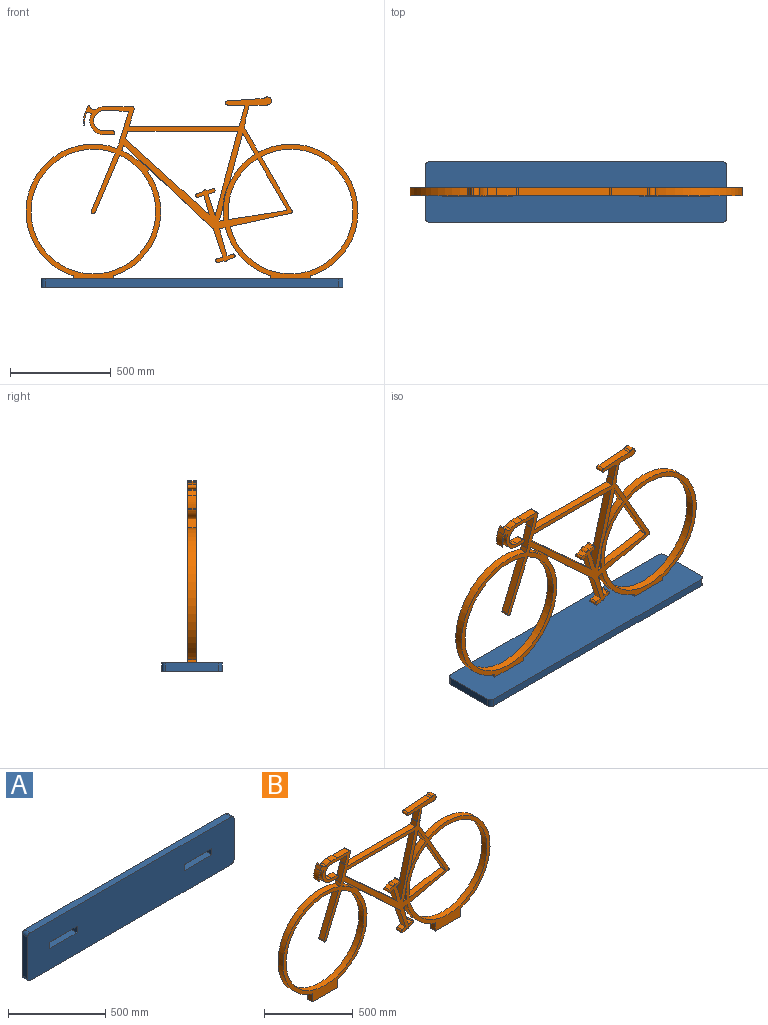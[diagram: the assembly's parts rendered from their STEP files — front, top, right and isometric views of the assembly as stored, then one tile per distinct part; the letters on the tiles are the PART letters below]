
ASSEMBLY  parts=2 mates=1
PART A: 18 faces, bbox 1500x40x300 mm
  f0: plane 200x40mm, normal (0,0,-1), area 8000mm2, adj f1,f15,f16,f17
  f1: plane 40x40mm, normal (-1,0,0), area 1600mm2, adj f0,f2,f16,f17
  f2: plane 200x40mm, normal (0,0,1), area 8000mm2, adj f1,f15,f16,f17
  f3: plane 1460x40mm, normal (0,0,-1), area 58400mm2, adj f4,f13,f16,f17
  f4: cylinder r=20mm len=40mm, axis (0,1,0), area 1256.6mm2, adj f3,f5,f16,f17
  f5: plane 260x40mm, normal (1,0,0), area 10400mm2, adj f4,f6,f16,f17
  f6: cylinder r=20mm len=40mm, axis (0,1,0), area 1256.6mm2, adj f5,f7,f16,f17
  f7: plane 1460x40mm, normal (0,0,1), area 58400mm2, adj f6,f8,f16,f17
  f8: cylinder r=20mm len=40mm, axis (0,1,0), area 1256.6mm2, adj f7,f9,f16,f17
  f9: plane 260x40mm, normal (-1,0,0), area 10400mm2, adj f8,f13,f16,f17
  f10: plane 40x40mm, normal (-1,0,0), area 1600mm2, adj f11,f14,f16,f17
  f11: plane 200x40mm, normal (0,0,1), area 8000mm2, adj f10,f12,f16,f17
  f12: plane 40x40mm, normal (1,0,0), area 1600mm2, adj f11,f14,f16,f17
  f13: cylinder r=20mm len=40mm, axis (0,1,0), area 1256.6mm2, adj f3,f9,f16,f17
  f14: plane 200x40mm, normal (0,0,-1), area 8000mm2, adj f10,f12,f16,f17
  f15: plane 40x40mm, normal (1,0,0), area 1600mm2, adj f0,f2,f16,f17
  f16: plane 1500x300mm, normal (0,-1,0), area 433656.6mm2, adj f0,f1,f2,f3,f4,f5,f6,f7
  f17: plane 1500x300mm, normal (0,1,0), area 433656.6mm2, adj f0,f1,f2,f3,f4,f5,f6,f7
PART B: 105 faces, bbox 1650x40x944.4 mm
  f0: plane 299.62x65.43mm, normal (0.21,0,-0.98), area 12267.2mm2, adj f1,f102,f103,f104
  f1: cylinder r=9mm len=40mm, axis (0,1,0), area 905.8mm2, adj f0,f2,f103,f104
  f2: plane 266.74x152.85mm, normal (0.87,0,0.5), area 12297.2mm2, adj f1,f102,f103,f104
  f3: cylinder r=310mm len=620mm, axis (0,1,0), area 76908.3mm2, adj f4,f96,f103,f104
  f4: plane 286.93x116.93mm, normal (-0.93,0,0.38), area 12393.5mm2, adj f3,f5,f103,f104
  f5: cylinder r=10mm len=40mm, axis (0,1,0), area 1250.1mm2, adj f4,f96,f103,f104
  f6: plane 73.76x69.4mm, normal (-0.69,0,-0.73), area 4051.1mm2, adj f7,f97,f103,f104
  f7: plane 40x7.1mm, normal (-0.73,0,0.69), area 389.9mm2, adj f6,f8,f103,f104
  f8: cylinder r=335mm len=78.04mm, axis (0,1,0), area 3724.8mm2, adj f7,f97,f103,f104
  f9: plane 415.14x377.47mm, normal (0.67,0,0.74), area 22443.7mm2, adj f10,f98,f103,f104
  f10: plane 40x36.4mm, normal (0.96,0,-0.28), area 1517.5mm2, adj f9,f11,f103,f104
  f11: plane 545.63x40mm, normal (0,0,-1), area 21825.3mm2, adj f10,f12,f103,f104
  f12: plane 416.76x111.67mm, normal (-0.97,0,0.26), area 17258.5mm2, adj f11,f13,f103,f104
  f13: plane 104.98x40mm, normal (0.95,0,0.32), area 4426.6mm2, adj f12,f14,f103,f104
  f14: plane 40x27.55mm, normal (0.29,0,-0.96), area 1152.8mm2, adj f13,f15,f103,f104
  f15: cylinder r=10mm len=40mm, axis (0,1,0), area 1256.6mm2, adj f14,f16,f103,f104
  f16: plane 40x27.55mm, normal (-0.29,0,0.96), area 1152.8mm2, adj f15,f17,f103,f104
  f17: cylinder r=15mm len=40mm, axis (0,1,0), area 1009.3mm2, adj f16,f18,f103,f104
  f18: plane 40x27.55mm, normal (-0.29,0,0.96), area 1152.8mm2, adj f17,f19,f103,f104
  f19: cylinder r=10mm len=40mm, axis (0,1,0), area 1256.6mm2, adj f18,f20,f103,f104
  f20: plane 40x27.55mm, normal (0.29,0,-0.96), area 1152.8mm2, adj f19,f98,f103,f104
  f21: plane 235.63x62.8mm, normal (0.97,0,-0.26), area 9754.3mm2, adj f22,f99,f103,f104
  f22: plane 104.53x60.49mm, normal (-0.87,0,-0.5), area 4830.8mm2, adj f21,f23,f103,f104
  f23: cylinder r=335mm len=327.57mm, axis (0,1,0), area 15308.2mm2, adj f22,f24,f103,f104
  f24: plane 40x21.95mm, normal (-0.15,0,0.99), area 888.8mm2, adj f23,f25,f103,f104
  f25: plane 63.96x40mm, normal (0.97,0,-0.26), area 2647.9mm2, adj f24,f99,f103,f104
  f26: cylinder r=3mm len=40mm, axis (0,1,0), area 232.8mm2, adj f27,f100,f103,f104
  f27: plane 286.57x44.86mm, normal (-0.15,0,0.99), area 11602.5mm2, adj f26,f28,f103,f104
  f28: cylinder r=310mm len=302.05mm, axis (0,1,0), area 14106.7mm2, adj f27,f100,f103,f104
  f29: cylinder r=20mm len=40mm, axis (0,1,0), area 189.4mm2, adj f30,f101,f103,f104
  f30: plane 138.94x46.33mm, normal (-0.95,0,-0.32), area 5858.3mm2, adj f29,f31,f103,f104
  f31: plane 40x27.55mm, normal (-0.29,0,0.96), area 1152.8mm2, adj f30,f32,f103,f104
  f32: cylinder r=10mm len=40mm, axis (0,1,0), area 1256.6mm2, adj f31,f33,f103,f104
  f33: plane 40x27.55mm, normal (0.29,0,-0.96), area 1152.8mm2, adj f32,f34,f103,f104
  f34: cylinder r=15mm len=40mm, axis (0,1,0), area 1009.3mm2, adj f33,f35,f103,f104
  f35: plane 40x27.55mm, normal (0.29,0,-0.96), area 1152.8mm2, adj f34,f36,f103,f104
  f36: cylinder r=10mm len=40mm, axis (0,1,0), area 1256.6mm2, adj f35,f37,f103,f104
  f37: plane 40x27.55mm, normal (-0.29,0,0.96), area 1152.8mm2, adj f36,f38,f103,f104
  f38: plane 133.82x40mm, normal (0.96,0,0.27), area 5560.3mm2, adj f37,f39,f103,f104
  f39: plane 40x28.33mm, normal (0.21,0,-0.98), area 1159.9mm2, adj f38,f40,f103,f104
  f40: cylinder r=335mm len=240.06mm, axis (0,1,0), area 13769.4mm2, adj f39,f41,f103,f104
  f41: plane 55.27x40mm, normal (-1,0,0), area 2210.9mm2, adj f40,f42,f103,f104
  f42: plane 200x40mm, normal (0,0,-1), area 8000mm2, adj f41,f43,f103,f104
  f43: plane 55.27x40mm, normal (1,0,0), area 2210.9mm2, adj f42,f44,f103,f104
  f44: cylinder r=335mm len=654.73mm, axis (0,1,0), area 44661.5mm2, adj f43,f45,f103,f104
  f45: plane 123.92x71.01mm, normal (0.87,0,0.5), area 5713.1mm2, adj f44,f46,f103,f104
  f46: plane 40x29.62mm, normal (0.97,0,-0.26), area 1226mm2, adj f45,f47,f103,f104
  f47: plane 40x3.7mm, normal (0.26,0,0.97), area 153.2mm2, adj f46,f48,f103,f104
  f48: plane 78.52x40mm, normal (0.97,0,-0.24), area 3237.8mm2, adj f47,f49,f103,f104
  f49: cylinder r=2mm len=40mm, axis (0,1,0), area 106mm2, adj f48,f50,f103,f104
  f50: plane 89.34x40mm, normal (0,0,-1), area 3573.6mm2, adj f49,f51,f103,f104
  f51: cylinder r=20mm len=40mm, axis (0,1,0), area 3014.9mm2, adj f50,f52,f103,f104
  f52: cylinder r=20mm len=40mm, axis (0,1,0), area 445.9mm2, adj f51,f53,f103,f104
  f53: plane 178.62x40mm, normal (-0.07,0,1), area 7162.1mm2, adj f52,f54,f103,f104
  f54: cylinder r=10mm len=40mm, axis (0,1,0), area 1228.8mm2, adj f53,f55,f103,f104
  f55: plane 85.7x40mm, normal (0,0,-1), area 3428mm2, adj f54,f56,f103,f104
  f56: cylinder r=2mm len=40mm, axis (0,1,0), area 146.6mm2, adj f55,f57,f103,f104
  f57: plane 71.97x40mm, normal (-0.97,0,0.26), area 2980.3mm2, adj f56,f58,f103,f104
  f58: plane 40x1.51mm, normal (0.26,0,0.97), area 62.4mm2, adj f57,f59,f103,f104
  f59: plane 40x32.34mm, normal (-0.97,0,0.26), area 1339.3mm2, adj f58,f60,f103,f104
  f60: plane 544.98x40mm, normal (0,0,1), area 21799.2mm2, adj f59,f61,f103,f104
  f61: plane 40x11.4mm, normal (0.96,0,-0.28), area 475.2mm2, adj f60,f62,f103,f104
  f62: plane 40x0.76mm, normal (0.29,0,0.96), area 31.8mm2, adj f61,f63,f103,f104
  f63: plane 70.91x40mm, normal (0.96,0,-0.29), area 2965.9mm2, adj f62,f64,f103,f104
  f64: cylinder r=12mm len=40mm, axis (0,1,0), area 831.6mm2, adj f63,f65,f103,f104
  f65: plane 96.2x40mm, normal (0,0,1), area 3848.2mm2, adj f64,f66,f103,f104
  f66: plane 45.03x40mm, normal (0,0,1), area 1801.2mm2, adj f65,f67,f103,f104
  f67: cylinder r=70mm len=40mm, axis (0,1,0), area 1653.7mm2, adj f66,f68,f103,f104
  f68: cylinder r=25mm len=40mm, axis (0,1,0), area 1554.2mm2, adj f67,f69,f103,f104
  f69: cylinder r=4mm len=40mm, axis (0,1,0), area 371.9mm2, adj f68,f70,f103,f104
  f70: plane 40x24.76mm, normal (-0.9,0,0.43), area 1096.6mm2, adj f69,f71,f103,f104
  f71: cylinder r=110mm len=69.44mm, axis (0,1,0), area 2847.1mm2, adj f70,f72,f103,f104
  f72: cylinder r=2mm len=40mm, axis (0,1,0), area 271.9mm2, adj f71,f73,f103,f104
  f73: cylinder r=100mm len=60.22mm, axis (0,1,0), area 2490.8mm2, adj f72,f74,f103,f104
  f74: cylinder r=4mm len=40mm, axis (0,1,0), area 288.6mm2, adj f73,f75,f103,f104
  f75: plane 40x13.66mm, normal (-0.43,0,-0.9), area 605mm2, adj f74,f76,f103,f104
  f76: cylinder r=3mm len=40mm, axis (0,1,0), area 191.2mm2, adj f75,f77,f103,f104
  f77: cylinder r=70mm len=101.43mm, axis (0,1,0), area 5702.2mm2, adj f76,f78,f103,f104
  f78: plane 45x40mm, normal (0,0,-1), area 1800mm2, adj f77,f79,f103,f104
  f79: cylinder r=10mm len=40mm, axis (0,1,0), area 1256.6mm2, adj f78,f80,f103,f104
  f80: plane 45x40mm, normal (0,0,1), area 1800mm2, adj f79,f81,f103,f104
  f81: cylinder r=50mm len=100mm, axis (0,1,0), area 6283.2mm2, adj f80,f82,f103,f104
  f82: plane 45x40mm, normal (0,0,-1), area 1800mm2, adj f81,f83,f103,f104
  f83: plane 76.04x40mm, normal (-0.04,0,-1), area 3044.4mm2, adj f82,f84,f103,f104
  f84: cylinder r=2mm len=40mm, axis (0,1,0), area 145.9mm2, adj f83,f85,f103,f104
  f85: plane 47.81x40mm, normal (-0.96,0,0.29), area 1999.9mm2, adj f84,f86,f103,f104
  f86: plane 40x5.94mm, normal (-0.97,0,0.23), area 243.8mm2, adj f85,f87,f103,f104
  f87: plane 105.48x40mm, normal (-0.96,0,0.29), area 4411.8mm2, adj f86,f88,f103,f104
  f88: plane 40x22.19mm, normal (-0.93,0,0.38), area 958.6mm2, adj f87,f89,f103,f104
  f89: cylinder r=335mm len=654.73mm, axis (0,1,0), area 42820.7mm2, adj f88,f90,f103,f104
  f90: plane 55.27x40mm, normal (-1,0,0), area 2210.9mm2, adj f89,f91,f103,f104
  f91: plane 200x40mm, normal (0,0,-1), area 8000mm2, adj f90,f92,f103,f104
  f92: plane 55.55x40mm, normal (1,0,0), area 2222.2mm2, adj f91,f93,f103,f104
  f93: plane 40x4.26mm, normal (0.25,0,-0.97), area 175.6mm2, adj f92,f94,f103,f104
  f94: cylinder r=335mm len=519.67mm, axis (0,1,0), area 25446.1mm2, adj f93,f95,f103,f104
  f95: plane 40x10.44mm, normal (0.73,0,-0.69), area 573.1mm2, adj f94,f101,f103,f104
  f96: plane 284.98x121.61mm, normal (0.92,0,-0.39), area 12393.5mm2, adj f3,f5,f103,f104
  f97: plane 40x26.24mm, normal (0.92,0,-0.39), area 1137.3mm2, adj f6,f8,f103,f104
  f98: plane 95.53x40mm, normal (-0.96,0,-0.27), area 3969.2mm2, adj f9,f20,f103,f104
  f99: cylinder r=337.5mm len=135.94mm, axis (0,1,0), area 5669mm2, adj f21,f25,f103,f104
  f100: plane 252.72x146.26mm, normal (-0.87,0,-0.5), area 11679.8mm2, adj f26,f28,f103,f104
  f101: plane 314.83x296.2mm, normal (-0.69,0,-0.73), area 17290.5mm2, adj f29,f95,f103,f104
  f102: cylinder r=310mm len=620mm, axis (0,1,0), area 61537mm2, adj f0,f2,f103,f104
  f103: plane 1650x944.43mm, normal (0,-1,0), area 226890.1mm2, adj f0,f1,f2,f3,f4,f5,f6,f7
  f104: plane 1650x944.43mm, normal (0,1,0), area 226890.1mm2, adj f0,f1,f2,f3,f4,f5,f6,f7
PLACE A rot(axis=(-1,0,0),90deg) t=(-586.78,268.12,-795.27)mm
PLACE B t=(-363.52,-555.99,-490.27)mm
MATE fastened B.f91 <-> A.f17  axis (0,0,-1) through (-1069.76,-595.99,-795.27)mm
